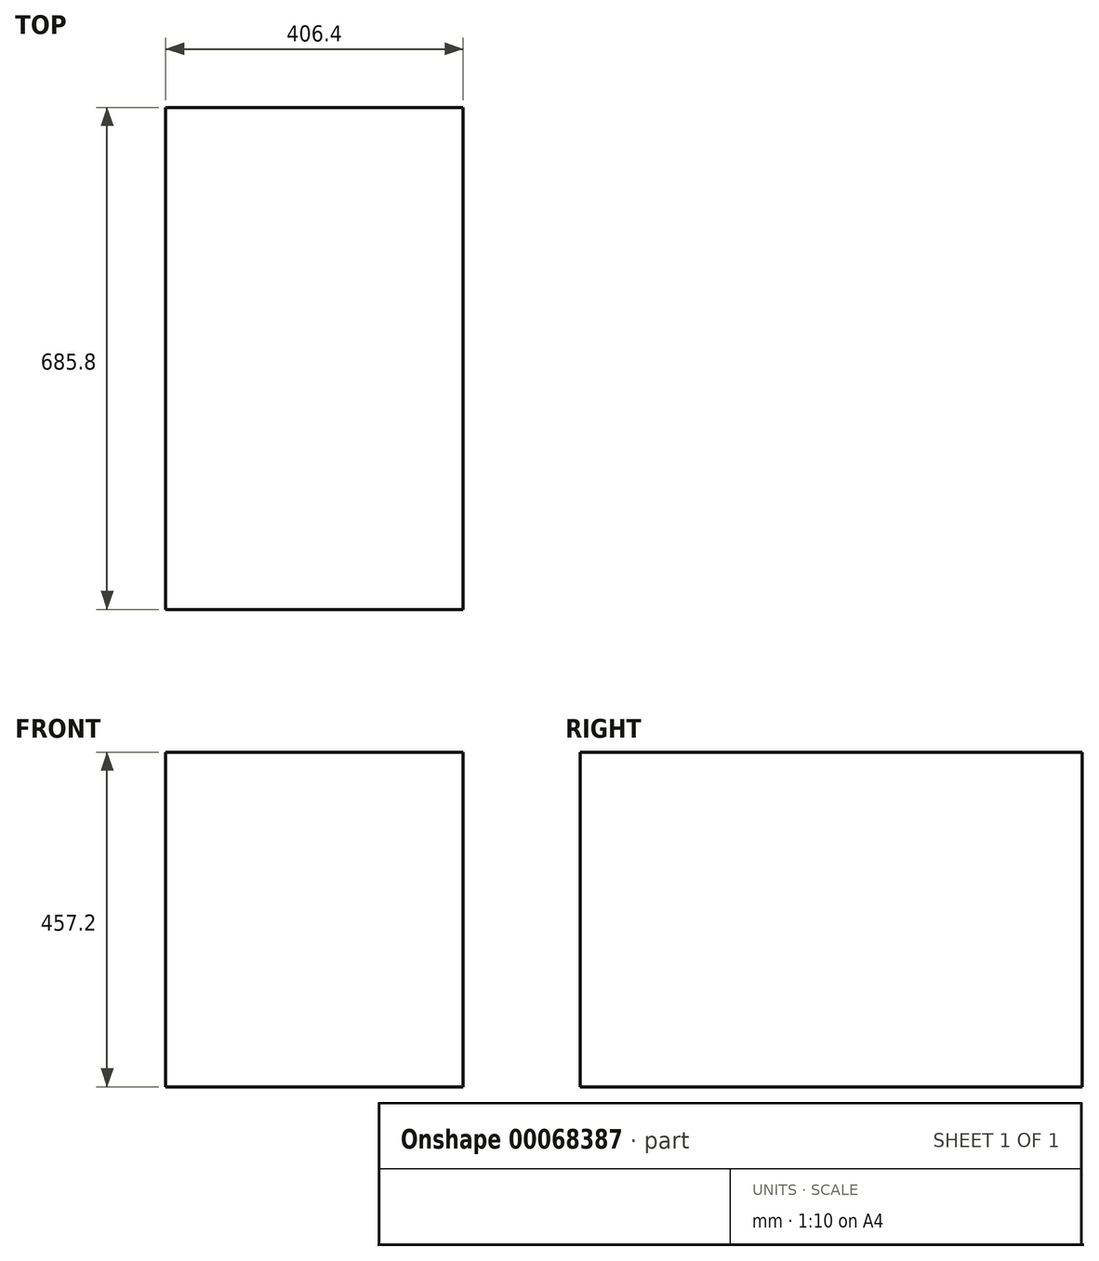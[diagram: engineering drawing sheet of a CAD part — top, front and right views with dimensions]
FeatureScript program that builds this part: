
annotation { "Feature Type Name" : "Feature", "Feature Type Description" : "" }
export const myFeature = defineFeature(function(context is Context, id is Id, definition is map)
    precondition{}
    {
        {
            var Q0;
            Q0=qCreatedBy(makeId("Top.planeOp"),FACE);
            var sketch = newSketch(context, id + "F0", { "sketchPlane" : qUnion([Q0])});
            skLineSegment(sketch, "E0.rect.bottom", {"start": v(203.2, 342.9) * mm, "end": v(-203.2, 342.9) * mm});
            skLineSegment(sketch, "E0.rect.top", {"start": v(203.2, -342.9) * mm, "end": v(-203.2, -342.9) * mm});
            skLineSegment(sketch, "E0.rect.left", {"start": v(203.2, 342.9) * mm, "end": v(203.2, -342.9) * mm});
            skLineSegment(sketch, "E0.rect.right", {"start": v(-203.2, 342.9) * mm, "end": v(-203.2, -342.9) * mm});
            skPoint(sketch, "E0.rect.middle", {"position": v(0, 0) * mm});
            skSolve(sketch);
        }
        {
            var Q0;
            Q0 = qSketchRegion(id + "F0", true);
            extrude(context, id + "F1", {"entities" : qUnion([Q0]), "depth" : 457.2 * mm});
        }
    });
